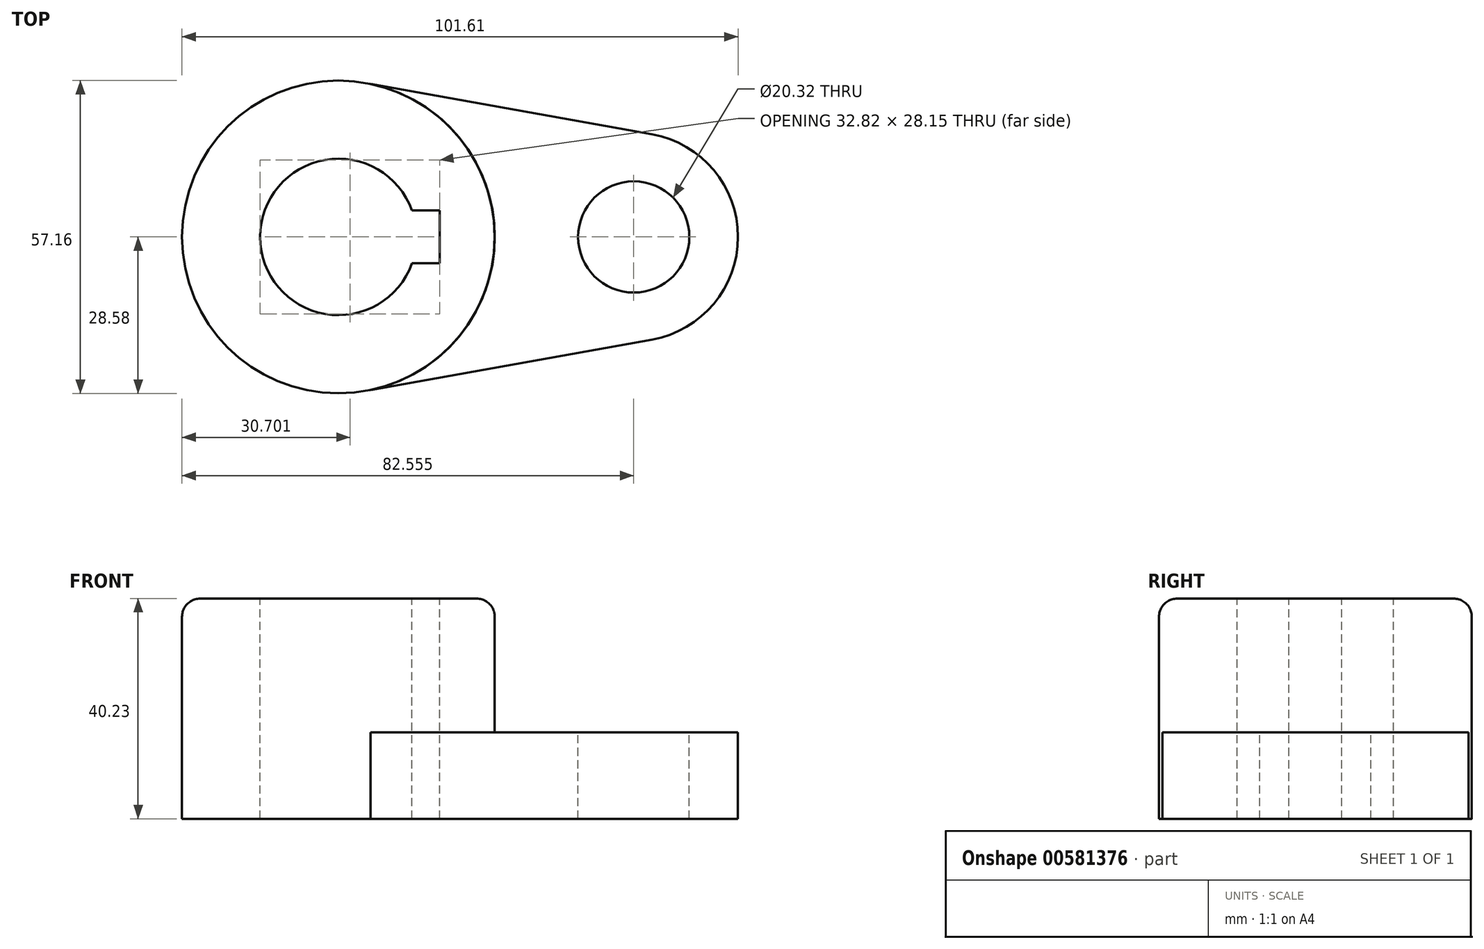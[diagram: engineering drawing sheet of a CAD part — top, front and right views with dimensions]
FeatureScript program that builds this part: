
annotation { "Feature Type Name" : "Feature", "Feature Type Description" : "" }
export const myFeature = defineFeature(function(context is Context, id is Id, definition is map)
    precondition{}
    {
        {
            var Q0;
            Q0=qCreatedBy(makeId("Top.planeOp"),FACE);
            var sketch = newSketch(context, id + "F0", { "sketchPlane" : qUnion([Q0])});
            skCircle(sketch, "E0", {"center": v(0, 0) * mm, "radius": 28.58 * mm});
            skCircle(sketch, "E1", {"center": v(53.98, 0) * mm, "radius": 19.05 * mm});
            skCircle(sketch, "E2", {"center": v(53.98, 0) * mm, "radius": 10.16 * mm});
            skLineSegment(sketch, "E3", {"start": v(4.2, 28.26) * mm, "end": v(57.33, 18.75) * mm});
            skLineSegment(sketch, "E4.MirrorCS", {"start": v(4.2, -28.26) * mm, "end": v(57.33, -18.75) * mm});
            skArc(sketch, "E5", {"start": v(13.45, 4.83) * mm, "mid": v(-14.29, 0) * mm, "end": v(13.45, -4.83) * mm});
            skLineSegment(sketch, "E6", {"start": v(13.45, 4.83) * mm, "end": v(18.53, 4.83) * mm});
            skLineSegment(sketch, "E7", {"start": v(13.45, -4.83) * mm, "end": v(18.53, -4.83) * mm});
            skPoint(sketch, "E8.start.orphan", {"position": v(-14.29, 0) * mm});
            skLineSegment(sketch, "E9", {"start": v(18.53, -4.83) * mm, "end": v(18.53, 4.83) * mm});
            skSolve(sketch);
        }
        {
            var Q0;
            Q0 = qSketchRegion(id + "F0", true);
            extrude(context, id + "F1", {"entities" : qUnion([Q0]), "oppositeDirection" : true, "depth" : 15.77 * mm, "offsetDistance" : 25.4 * mm});
        }
        {
            var Q0;
            Q0=makeQuery(id+"F1.opExtrude","CAP_FACE",FACE,{"disambiguationData":[OSD([sQuery(id+"F0.wireOp",EDGE,"E0"),sQuery(id+"F0.wireOp",EDGE,"E1"),sQuery(id+"F0.wireOp",EDGE,"E2"),sQuery(id+"F0.wireOp",EDGE,"E3"),sQuery(id+"F0.wireOp",EDGE,"E4.MirrorCS"),sQuery(id+"F0.wireOp",EDGE,"E5"),sQuery(id+"F0.wireOp",EDGE,"E6"),sQuery(id+"F0.wireOp",EDGE,"E7"),sQuery(id+"F0.wireOp",EDGE,"E9")])],"isStart":true});
            var sketch = newSketch(context, id + "F2", { "sketchPlane" : qUnion([Q0])});
            skArc(sketch, "E10.0", {"start": v(5.87, 27.97) * mm, "mid": v(-28.58, 0) * mm, "end": v(5.87, -27.97) * mm});
            skLineSegment(sketch, "E11.0", {"start": v(5.87, 27.97) * mm, "end": v(57.33, 18.75) * mm});
            skArc(sketch, "E12.0", {"start": v(13.45, 4.83) * mm, "mid": v(-14.29, 0) * mm, "end": v(13.45, -4.83) * mm});
            skPoint(sketch, "E13.0", {"position": v(15.99, 4.83) * mm});
            skLineSegment(sketch, "E14.0", {"start": v(18.53, -4.83) * mm, "end": v(18.53, 4.83) * mm});
            skPoint(sketch, "E15.0", {"position": v(15.99, -4.83) * mm});
            skLineSegment(sketch, "E16.0", {"start": v(5.87, -27.97) * mm, "end": v(57.33, -18.75) * mm});
            skCircle(sketch, "E17", {"center": v(0, 0) * mm, "radius": 28.58 * mm});
            skLineSegment(sketch, "E18", {"start": v(13.45, 4.83) * mm, "end": v(18.53, 4.83) * mm});
            skLineSegment(sketch, "E19", {"start": v(18.53, -4.83) * mm, "end": v(13.45, -4.83) * mm});
            skSolve(sketch);
        }
        {
            var Q0;
            Q0=makeQuery(id+"F2.imprint","IMPRINT",FACE,{"disambiguationData":[TD([[makeQuery(id+"F2.imprint","IMPRINT",EDGE,{"derivedFrom":sQuery(id+"F2.wireOp",EDGE,"E14.0")}),-1.0]])]});
            extrude(context, id + "F3", {"entities" : qUnion([Q0]), "operationType" : NewBodyOperationType.ADD, "depth" : 24.46 * mm, "offsetDistance" : 25.4 * mm});
        }
        {
            var Q0;
            Q0=makeQuery(id+"F3.opExtrude","CAP_EDGE",EDGE,{"disambiguationData":[OSD([sQuery(id+"F2.wireOp",EDGE,"E17")])],"isStart":false});
            fillet(context, id + "F4", {"entities" : qUnion([Q0]), "radius" : 3.3 * mm, "tangentPropagation" : true, "allowEdgeOverflow" : false});
        }
    });
